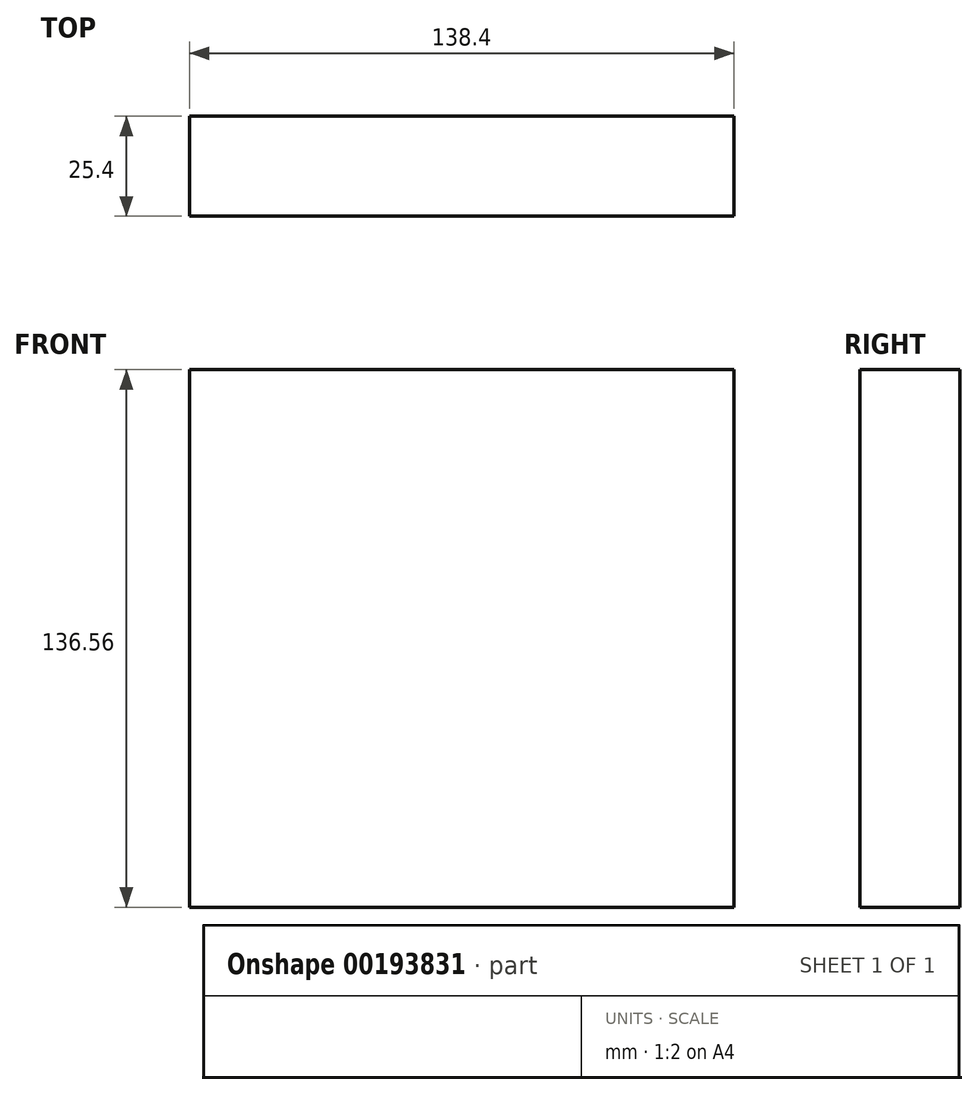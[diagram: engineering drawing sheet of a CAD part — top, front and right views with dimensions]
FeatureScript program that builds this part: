
annotation { "Feature Type Name" : "Feature", "Feature Type Description" : "" }
export const myFeature = defineFeature(function(context is Context, id is Id, definition is map)
    precondition{}
    {
        {
            var Q0;
            Q0=qCreatedBy(makeId("Front.planeOp"),FACE);
            var sketch = newSketch(context, id + "F0", { "sketchPlane" : qUnion([Q0])});
            skLineSegment(sketch, "E0.bottom", {"start": v(-69.2, 68.28) * mm, "end": v(69.2, 68.28) * mm});
            skLineSegment(sketch, "E0.top", {"start": v(-69.2, -68.28) * mm, "end": v(69.2, -68.28) * mm});
            skLineSegment(sketch, "E0.left", {"start": v(-69.2, 68.28) * mm, "end": v(-69.2, -68.28) * mm});
            skLineSegment(sketch, "E0.right", {"start": v(69.2, 68.28) * mm, "end": v(69.2, -68.28) * mm});
            skPoint(sketch, "E0.middle", {"position": v(0, 0) * mm});
            skSolve(sketch);
        }
        {
            var Q0;
            Q0=makeQuery(id+"F0.imprint","IMPRINT",FACE,{"disambiguationData":[TD([[makeQuery(id+"F0.imprint","IMPRINT",EDGE,{"derivedFrom":sQuery(id+"F0.wireOp",EDGE,"E0.bottom")}),-1.0]])]});
            extrude(context, id + "F1", {"entities" : qUnion([Q0]), "depth" : 25.4 * mm});
        }
        {
            var Q0;
            Q0=qCreatedBy(makeId("Front.planeOp"),FACE);
            var sketch = newSketch(context, id + "F2", { "sketchPlane" : qUnion([Q0])});
            skCircle(sketch, "E1", {"center": v(0, 0) * mm, "radius": 68 * mm});
            skSolve(sketch);
        }
        {
            var Q0;
            Q0=sQuery(id+"F2.wireOp",EDGE,"E1");
            extrude(context, id + "F3", {"bodyType" : ToolBodyType.SURFACE, "surfaceEntities" : qUnion([Q0]), "depth" : 38.1 * mm});
        }
        {
            var Q0;
            Q0=qCreatedBy(makeId("Front.planeOp"),FACE);
            var sketch = newSketch(context, id + "F4", { "sketchPlane" : qUnion([Q0])});
            skLineSegment(sketch, "E2.bottom", {"start": v(-49.12, 46.65) * mm, "end": v(49.12, 46.65) * mm});
            skLineSegment(sketch, "E2.top", {"start": v(-49.12, -46.65) * mm, "end": v(49.12, -46.65) * mm});
            skLineSegment(sketch, "E2.left", {"start": v(-49.12, 46.65) * mm, "end": v(-49.12, -46.65) * mm});
            skLineSegment(sketch, "E2.right", {"start": v(49.12, 46.65) * mm, "end": v(49.12, -46.65) * mm});
            skPoint(sketch, "E2.middle", {"position": v(0, 0) * mm});
            skSolve(sketch);
        }
        {
            var Q0;
            Q0=sQuery(id+"F4.wireOp",EDGE,"E2.bottom");
            var Q1;
            Q1=sQuery(id+"F4.wireOp",EDGE,"E2.left");
            var Q2;
            Q2=sQuery(id+"F4.wireOp",EDGE,"E2.right");
            var Q3;
            Q3=sQuery(id+"F4.wireOp",EDGE,"E2.top");
            extrude(context, id + "F5", {"bodyType" : ToolBodyType.SURFACE, "surfaceEntities" : qUnion([Q0, Q1, Q2, Q3]), "depth" : 50.8 * mm});
        }
        {
            var Q0;
            Q0=qCreatedBy(makeId("Front.planeOp"),FACE);
            var sketch = newSketch(context, id + "F6", { "sketchPlane" : qUnion([Q0])});
            skCircle(sketch, "E3", {"center": v(0, 0) * mm, "radius": 44.67 * mm});
            skSolve(sketch);
        }
        {
            var Q0;
            Q0=sQuery(id+"F6.wireOp",EDGE,"E3");
            extrude(context, id + "F7", {"bodyType" : ToolBodyType.SURFACE, "surfaceEntities" : qUnion([Q0]), "depth" : 63.5 * mm});
        }
    });
